# Revit family: 2-5156-124 Pebble
name_source: partatom
category: Lighting Fixtures
revit_build: Autodesk Revit LT 2014 (Build: 20130308_1515(x64)
units: mm (PartAtom-declared; Revit-internal decimal feet)

## types (1)
- 2-5156-124 Pebble
    Apparent Load = 17 VA
    Ballast Manufacturer = Antron Electronics CSD-UV18P
    Color Filter = 16777215
    Default Elevation = 4' - 0"
    Description = 12" Contemporary Wall Sconce
    Diffuser = 1-White Opal Glass
    Dimming Lamp Color Temperature Shift = <None>
    Emit Shape Visible in Rendering = No
    Emit from Rectangle Length = 4' - 0"
    Emit from Rectangle Width = 2' - 0"
    Fixture Height = 1' - 0 25/32"
    Fixture Width = 0' - 6 3/16"
    Input Power = 16.8 W
    Input Voltage = 120 V
    Junction Box = 4" Octagonal
    Lamp = 1x18W Double Twin Tube Compact Fluorescent
    Lamp Manufacturer = Sylvania
    Manufacturer = Oxygen Lighting
    Metal Finish = 24 -Satin Nickel
    Model = 2-5156-124
    Photometric Web File = 2-5156-124 Pebble ITL77192.IES
    Power Factor = 0.99
    Product Documentation Link = http://oxygenlighting.com.s3.amazonaws.com
    Tilt Angle = -90.00°
    Type Comments = Lighting - Fluorescent
    URL = http://www.oxygenlighting.com

## geometry (parser evidence)
native form markers: Sweep x1
no freeform markers — native parametric forms only
